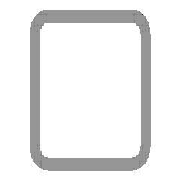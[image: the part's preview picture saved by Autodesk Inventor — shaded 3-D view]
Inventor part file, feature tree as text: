
AUTODESK INVENTOR PART (.ipt)
format: ipt  version: 2022 (Build 260153000, 153)  size: 250,368 bytes
history: native  units: mm (DEFAULTED — no unit token found)
features: other x7, sketch x3, surface_op x2, plane x1
ambient origin geometry x8: Origin, YZ Plane, XZ Plane, XY Plane, X Axis, Y Axis, Z Axis, Center Point
bodies: Solid1 (feature_tree), Body (feature_tree), Solid3 (feature_tree)
feature tree (13):
  parser-record x1  (decoder bookkeeping rows leaked as tree rows — omitted from the tree; the rows remain in map.json)
  other  "Driven Length"
  other  "Start Plane"
  other  "End Plane"
  sketch  "Sketch"  dims[d7=7.5mm d10=40.0mm d11=40.0mm d12=5.0mm d13=12.5mm d14=167.5mm d15=20.0mm d16=20.0mm d17=90.0deg d18=155.0mm d37=5.0mm d38=5.0mm d39=5.0mm d40=5.0mm d41=5.0mm d42=5.0mm d43=5.0mm d44=5.0mm d45=0.0mm d46=5.0mm d47=5.0mm d48=5.0mm d49=5.0mm d50=5.0mm d51=5.0mm d52=5.0mm d53=5.0mm d54=0.0mm]
  sketch  "Sketch3"  dims[d3=155.0mm]
  plane  "Work Plane3"
  sketch  "Sketch4"  dims[d4=0.0mm]
  other  "Srf5"
  other  "Srf6"
  other  "Srf4"
  surface_op  "Boundary Patch3"
  surface_op  "Boundary Patch4"
